# Revit family: DBLTD_TheSenatorGroup_OffcTbls_Play_AVMedia_US
name_source: partatom
category: Furniture
revit_build: Autodesk Revit 2018 (Build: 20170223_1515(x64)
units: mm (PartAtom-declared; Revit-internal decimal feet)

## family parameters
Always vertical = Yes
Cut with Voids When Loaded = No
Room Calculation Point = No
Shared = Yes
Work Plane-Based = No

## types (2) — shared parameters
AssetType = Movable
BIMObjectName = TheSenatorGroup_OfficeTables_Play_AVMedia
Category = Pr_40_50_21_60:Office tables
DimensionsHeight = 29" - 48"
DimensionsPlanSize = 48" x 90"
DurationUnit = Years
ExpectedLife = 15
ExposedEdges = Matching
Finish = HD Highland Oak, BH Beech, MP Maple, WH White, AT Autumn. WK Winter Oak, SO Strata Oak, MC Mocha, HW Hacienda White, DN Denim, LY Clay, LS Lemon Sorbet, LG Light Grey, CW Carini Walnut
FrameSupports = Adjustable
FramesColour = Black
IfcExportAs = IfcFurnitureType
IfcExportType = TABLE
Keynote = Pr_40_50_21_60
Manufacturer = The Senator Group
ManufacturerName = The Senator Group
ManufacturerURL = https://www.thesenatorgroup.com
Material = MFC
NBSDescription = Office tables
NBSReference = 45-35-20/340
Name = OfficeTables_Play_AVMedia_TheSenatorGroup
NominalDepth = 89 "
NominalHeight = 71 "
NominalLength = 47 "
NominalWidth = 47 "
NumberOfChairs = 5
OmniClassCode = 22-12 51 23
OmniClassTitle = Office Tables
OmniClassVersion = Table 22 2012-05-16
ProductInformation = https://www.thesenatorgroup.com
ReplacementCost = 0
Shape = Rectangular
Size = L 90" x  W 48" x  H 29" - 48"
TableTopThickness = 1 "
URL = https://www.thesenatorgroup.com
Uniclass2015Code = Pr_40_50_21_60
Uniclass2015Title = Office tables
Uniclass2015Version = Products v1.9
Version = 1
WarrantyDescription = Senator warrants that its manufactured products are free from manufacturing defects - in materials or workmanship - for a period of ten (10) years on Senator Seating ranges; and fifteen (15) years on Senator Desking ranges
WarrantyDurationLabor = 15
WarrantyDurationParts = 15
WarrantyDurationUnit = Years
WarrantyGuarantorLabor = 15
WarrantyGuarantorParts = 15
WorksurfaceArea = 2.71 m²
zero-valued in all types: Cost

## per-type parameters (varying)
| type | Description | Features | Model | ModelNumber | ModelReference | WithCutout |
| AV Media with Cutout 48"(w) x 90"(d) x 29"- 48"(h) | 48" x 90" AV Media Table with Cutout | Height Adjustable, with cutout for IDP | PYPAE904850 + PYPUSIDP50AV or PYPUSIDP50AVS | PYPAE904850 + PYPUSIDP50AV or PYPUSIDP50AVS | AV Media with Cutout 48" (w) x 90"(d) x 29" - 48" (h) | Yes |
| AV Media 48"(w) x 90"(d) x 29"- 48"(h) | 48" x 90" AV Media Table | Height Adjustable | PYPAE9048 | PYPAE9048 | AV Media 48" (w) x 90"(d) x 29" - 48" (h) | No |

## geometry (parser evidence)
native form markers: Sweep x2
no freeform markers — native parametric forms only
